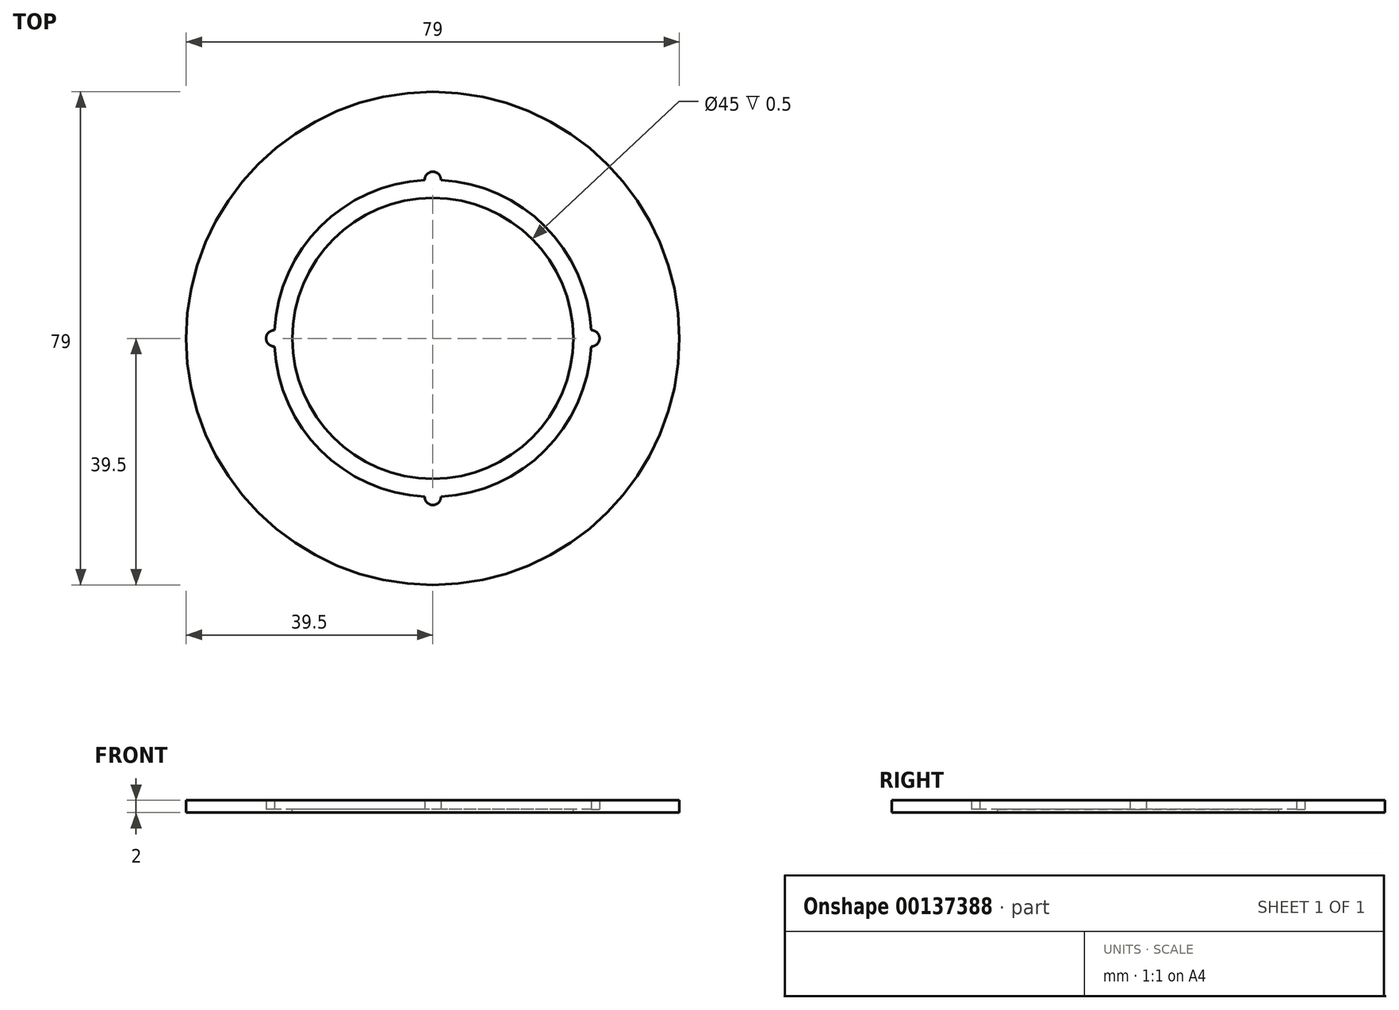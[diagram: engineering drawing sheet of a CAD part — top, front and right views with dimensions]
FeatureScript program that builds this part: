
annotation { "Feature Type Name" : "Feature", "Feature Type Description" : "" }
export const myFeature = defineFeature(function(context is Context, id is Id, definition is map)
    precondition{}
    {
        {
            var Q0;
            Q0=qCreatedBy(makeId("Front.planeOp"),FACE);
            var sketch = newSketch(context, id + "F0", { "sketchPlane" : qUnion([Q0])});
            skLineSegment(sketch, "E0", {"start": v(-39.5, 0) * mm, "end": v(-22.5, 0) * mm});
            skLineSegment(sketch, "E1", {"start": v(-22.5, 0) * mm, "end": v(-22.5, 0.5) * mm});
            skLineSegment(sketch, "E2", {"start": v(-22.5, 0.5) * mm, "end": v(-25.4, 0.5) * mm});
            skLineSegment(sketch, "E3", {"start": v(-25.4, 0.5) * mm, "end": v(-25.4, 2) * mm});
            skLineSegment(sketch, "E4", {"start": v(-25.4, 2) * mm, "end": v(-34.45, 2) * mm});
            skLineSegment(sketch, "E5", {"start": v(-34.45, 2) * mm, "end": v(-34.45, 2) * mm});
            skLineSegment(sketch, "E6", {"start": v(-34.45, 2) * mm, "end": v(-39.5, 2) * mm});
            skLineSegment(sketch, "E7", {"start": v(-39.5, 2) * mm, "end": v(-39.5, 0) * mm});
            skLineSegment(sketch, "E8", {"start": v(0, 24.49) * mm, "end": v(0, -14.91) * mm});
            skSolve(sketch);
        }
        {
            var Q0;
            Q0=makeQuery(id+"F0.imprint","IMPRINT",FACE,{"disambiguationData":[TD([[makeQuery(id+"F0.imprint","IMPRINT",EDGE,{"derivedFrom":sQuery(id+"F0.wireOp",EDGE,"E0")}),1.0]])]});
            var Q1;
            Q1=sQuery(id+"F0.wireOp",EDGE,"E8");
            revolve(context, id + "F1", {"entities" : qUnion([Q0]), "axis" : qUnion([Q1]), "revolveType" : RevolveType.FULL});
        }
        {
            var Q0;
            Q0=qCreatedBy(makeId("Top.planeOp"),FACE);
            var sketch = newSketch(context, id + "F2", { "sketchPlane" : qUnion([Q0])});
            skCircle(sketch, "E9", {"center": v(0, 25.4) * mm, "radius": 1.3 * mm});
            skCircle(sketch, "E10.1.0", {"center": v(-25.4, 0) * mm, "radius": 1.3 * mm});
            skCircle(sketch, "E10.2.0", {"center": v(0, -25.4) * mm, "radius": 1.3 * mm});
            skCircle(sketch, "E10.3.0", {"center": v(25.4, 0) * mm, "radius": 1.3 * mm});
            skPoint(sketch, "E10.center", {"position": v(0, 0) * mm});
            skSolve(sketch);
        }
        {
            var Q0;
            Q0=qSketchRegion(id+"F2",true);
            var Q1;
            Q1=makeQuery(id+"F1.opRevolve","SWEPT_FACE",FACE,{"disambiguationData":[OSD([sQuery(id+"F0.wireOp",EDGE,"E4"),sQuery(id+"F0.wireOp",EDGE,"E6")])]});
            extrude(context, id + "F3", {"entities" : qUnion([Q0]), "operationType" : NewBodyOperationType.REMOVE, "endBound" : BoundingType.UP_TO_SURFACE, "endBoundEntityFace" : qUnion([Q1]), "depth" : 5 * mm, "hasSecondDirection" : true, "secondDirectionOppositeDirection" : false, "secondDirectionDepth" : 0.5 * mm});
        }
    });
